# Revit family: Sink-Vessel-Lavatory-KOHLER-Veil-K-77171IN_1
name_source: partatom
category: Plumbing Fixtures
units: mm (PartAtom-declared; Revit-internal decimal feet)

## family parameters
Cut with Voids When Loaded = No
Host = Face
Maintain Annotation Orientation = No
OmniClass Number = 23.31.13.00
Part Type = Normal
Room Calculation Point = No
Round Connector Dimension = Use Diameter
Shared = No

## types (4) — shared parameters
ADA Compliant = No
Assembly Code = D2010400
CW Connection = No
Cold Water Inlet = Cold Water Inlet
Date Modified = 01/21/2025
Default Elevation = 36"
Description = Vessel Without Faucet Hole
Drain Included = No
HW Connection = No
Height = 8 1/4"
Hot Water Inlet = Hot Water Inlet
Length = 17 11/16"
Manufacturer = Kohler Co.
Master Format 2014 = 22 41 16
Master Format 2014 Name = Residential Lavatories and Sinks
Material = Vitreous China
Product Documentation Link = http://resources.kohler.com
Product Name = Veil
URL = https://www.kohler.co.in
Vent Connection = No
Waste Connection = Yes
Waste Water Outlet = Waste Water Outlet
WaterSense Certified = No
Width = 23 1/4"

## per-type parameters (varying)
| type | Finish | Model | Product Page URL | Type |
| 0-White | Kohler-Vitreous_China-0-White | K-77171IN-0 | https://www.kohler.co.in | 1 |
| 7-Black Black | Kohler-Vitreous_China-7-Black_Black | K-77171IN-7 | https://www.kohler.co.in | 2 |
| 58-Thunder Grey | Kohler-Vitreous_China-58-Thunder_Grey | K-77171IN-58 |  | 3 |
| DGS-Indigo | KOHLER-Vitreous_China-DGS-Indigo | K-77171IN-DGS | https://www.kohler.co.in | 4 |

## geometry (parser evidence)
native form markers: Sweep x4
no freeform markers — native parametric forms only
